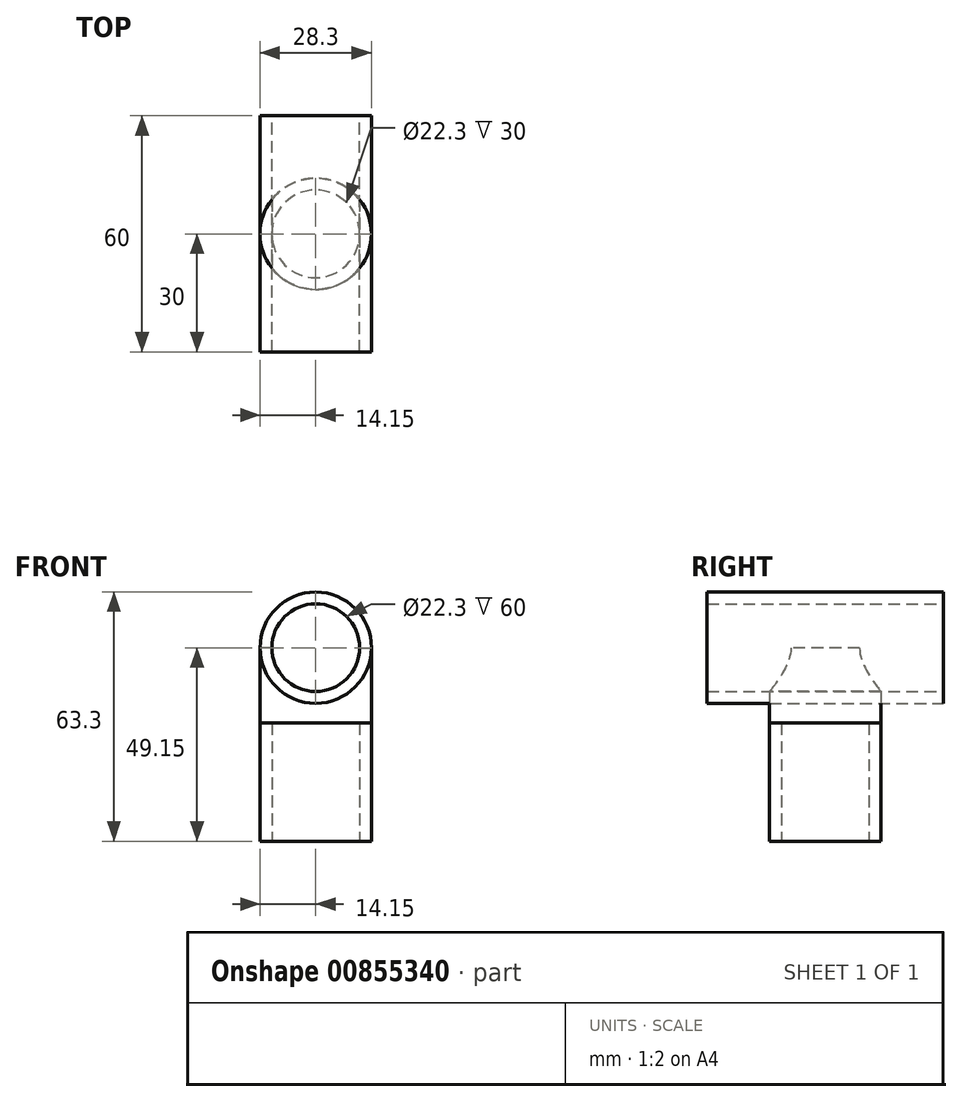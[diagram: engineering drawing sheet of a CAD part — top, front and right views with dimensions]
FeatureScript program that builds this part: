
annotation { "Feature Type Name" : "Feature", "Feature Type Description" : "" }
export const myFeature = defineFeature(function(context is Context, id is Id, definition is map)
    precondition{}
    {
        {
            var Q0;
            Q0=qCreatedBy(makeId("Top.planeOp"),FACE);
            var sketch = newSketch(context, id + "F0", { "sketchPlane" : qUnion([Q0])});
            skCircle(sketch, "E0", {"center": v(0, 0) * mm, "radius": 11.15 * mm});
            skCircle(sketch, "E1", {"center": v(0, 0) * mm, "radius": 14.15 * mm});
            skSolve(sketch);
        }
        {
            var Q0;
            Q0 = qSketchRegion(id + "F0", true);
            extrude(context, id + "F1", {"entities" : qUnion([Q0]), "depth" : 30 * mm, "offsetDistance" : 25 * mm});
        }
        {
            var Q0;
            Q0=qCreatedBy(makeId("Front.planeOp"),FACE);
            var sketch = newSketch(context, id + "F2", { "sketchPlane" : qUnion([Q0])});
            skLineSegment(sketch, "E2", {"start": v(0, 0) * mm, "end": v(0, 35) * mm, "construction": true});
            skLineSegment(sketch, "E3", {"start": v(0, 35) * mm, "end": v(0, 49.15) * mm, "construction": true});
            skCircle(sketch, "E4", {"center": v(0, 49.15) * mm, "radius": 14.15 * mm});
            skCircle(sketch, "E5", {"center": v(0, 49.15) * mm, "radius": 11.15 * mm});
            skSolve(sketch);
        }
        {
            var Q0;
            Q0 = qSketchRegion(id + "F2", true);
            extrude(context, id + "F3", {"entities" : qUnion([Q0]), "operationType" : NewBodyOperationType.ADD, "endBound" : BoundingType.SYMMETRIC, "depth" : 60 * mm, "offsetDistance" : 25 * mm});
        }
        {
            var Q0;
            Q0=makeQuery(id+"F1.opExtrude","CAP_FACE",FACE,{"disambiguationData":[OSD([sQuery(id+"F0.wireOp",EDGE,"E0"),sQuery(id+"F0.wireOp",EDGE,"E1")])],"isStart":false});
            var sketch = newSketch(context, id + "F4", { "sketchPlane" : qUnion([Q0])});
            skCircle(sketch, "E6", {"center": v(0, 0) * mm, "radius": 14.15 * mm});
            skSolve(sketch);
        }
        {
            var Q0;
            Q0 = qSketchRegion(id + "F4", true);
            extrude(context, id + "F5", {"entities" : qUnion([Q0]), "depth" : ((22.3 / 2) + 8) * mm, "offsetDistance" : 25 * mm});
        }
        {
            var Q0;
            Q0=makeQuery(id+"F3.opExtrude","CAP_FACE",FACE,{"disambiguationData":[OSD([sQuery(id+"F2.wireOp",EDGE,"E4"),sQuery(id+"F2.wireOp",EDGE,"E5")])],"isStart":false});
            var sketch = newSketch(context, id + "F6", { "sketchPlane" : qUnion([Q0])});
            skCircle(sketch, "E7", {"center": v(0, 49.15) * mm, "radius": 11.15 * mm});
            skSolve(sketch);
        }
        {
            var Q0;
            Q0 = qSketchRegion(id + "F6", true);
            extrude(context, id + "F7", {"entities" : qUnion([Q0]), "operationType" : NewBodyOperationType.REMOVE, "oppositeDirection" : true, "depth" : 60 * mm, "offsetDistance" : 25 * mm});
        }
    });
